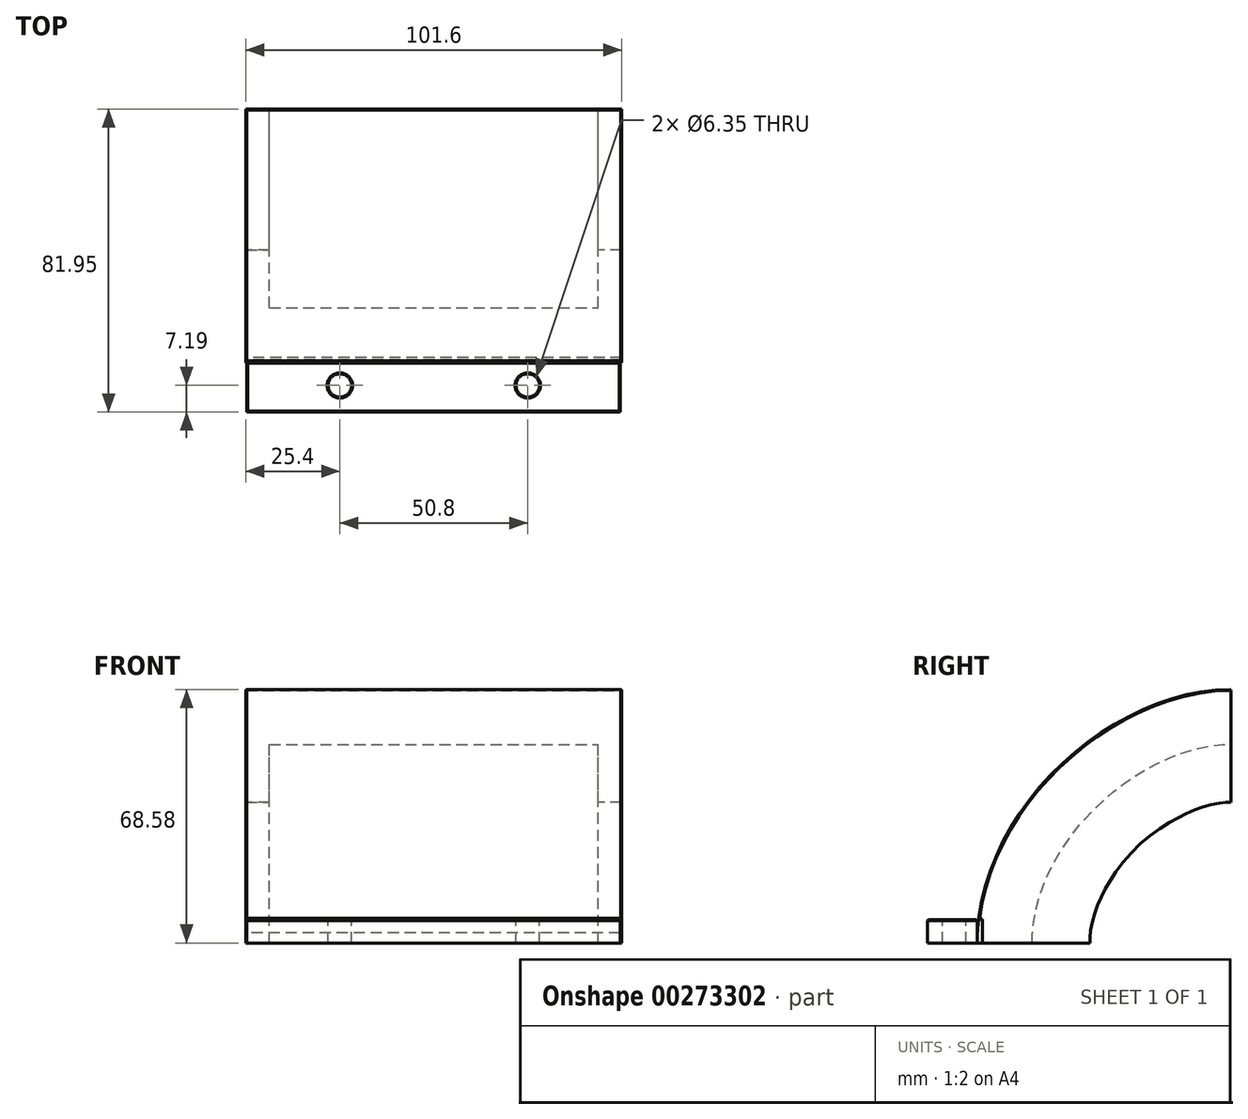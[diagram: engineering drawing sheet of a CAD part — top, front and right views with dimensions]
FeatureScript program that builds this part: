
annotation { "Feature Type Name" : "Feature", "Feature Type Description" : "" }
export const myFeature = defineFeature(function(context is Context, id is Id, definition is map)
    precondition{}
    {
        {
            var Q0;
            Q0=qCreatedBy(makeId("Right.planeOp"),FACE);
            var sketch = newSketch(context, id + "F0", { "sketchPlane" : qUnion([Q0])});
            skLineSegment(sketch, "E0", {"start": v(-36.59, 0) * mm, "end": v(-6.1, 0) * mm});
            skFitSpline(sketch, "E1", {"points": [v(-36.59, 0) * mm, v(32, 68.58) * mm], "startDerivative": vector(0.81, 109.5) * mm, "endDerivative": vector(95.98, 0.55) * mm});
            skLineSegment(sketch, "E2.bottom", {"start": v(-59.36, 6.45) * mm, "end": v(-35.21, 6.45) * mm});
            skLineSegment(sketch, "E2.top", {"start": v(-59.36, 0) * mm, "end": v(-35.21, 0) * mm});
            skLineSegment(sketch, "E2.left", {"start": v(-59.36, 6.45) * mm, "end": v(-59.36, 0) * mm});
            skLineSegment(sketch, "E2.right", {"start": v(-35.21, 6.45) * mm, "end": v(-35.21, 0) * mm});
            skFitSpline(sketch, "E3.0", {"points": [v(-6.1, -0.23) * mm, v(-6.1, 0.8) * mm, v(-5.96, 2.87) * mm, v(-5.36, 6.07) * mm, v(-4.35, 9.39) * mm, v(-2.9, 12.78) * mm, v(-1.04, 16.2) * mm, v(2, 20.7) * mm, v(6.72, 26.07) * mm, v(12.3, 30.58) * mm, v(16.95, 33.47) * mm, v(20.42, 35.23) * mm, v(23.8, 36.57) * mm, v(26.95, 37.49) * mm, v(29.8, 38) * mm, v(31.43, 38.1) * mm, v(32.17, 38.1) * mm]});
            skLineSegment(sketch, "E4", {"start": v(32, 38.1) * mm, "end": v(32, 68.58) * mm});
            skFitSpline(sketch, "E5.0", {"points": [v(-21.74, -0.11) * mm, v(-21.73, 0.72) * mm, v(-21.67, 2.4) * mm, v(-21.42, 4.89) * mm, v(-21.02, 7.37) * mm, v(-20.3, 10.68) * mm, v(-19.04, 14.78) * mm, v(-16.98, 19.63) * mm, v(-14.83, 23.56) * mm, v(-12.87, 26.62) * mm, v(-11.28, 28.87) * mm, v(-9.59, 31.06) * mm, v(-7.8, 33.18) * mm, v(-5.91, 35.22) * mm, v(-3.93, 37.2) * mm, v(-1.88, 39.09) * mm, v(0.24, 40.88) * mm, v(2.42, 42.57) * mm, v(4.66, 44.17) * mm, v(6.95, 45.66) * mm, v(9.26, 47.03) * mm, v(11.6, 48.28) * mm, v(14.74, 49.8) * mm, v(18.67, 51.36) * mm, v(22.54, 52.49) * mm, v(25.57, 53.12) * mm, v(27.8, 53.46) * mm, v(29.98, 53.67) * mm, v(31.38, 53.72) * mm, v(32.08, 53.73) * mm]});
            skSolve(sketch);
        }
        {
            var Q0;
            {var subQ0=sQuery(id+"F0.wireOp",EDGE,"E2.right");Q0=makeQuery(id+"F0.imprint","IMPRINT",FACE,{"disambiguationData":[TD([[makeQuery(id+"F0.imprint","IMPRINT",EDGE,{"derivedFrom":subQ0}),1.0]])]});}
            var Q1;
            {var subQ0=sQuery(id+"F0.wireOp",EDGE,"E3.0");var subQ1=sQuery(id+"F0.wireOp",EDGE,"E0");var subQ2=makeQuery(id+"F0.imprint","INTERSECT",VERTEX,{"derivedFrom":[subQ1,subQ0]});Q1=makeQuery(id+"F0.imprint","IMPRINT",FACE,{"disambiguationData":[TD([[makeQuery(id+"F0.imprint","IMPRINT",EDGE,{"disambiguationData":[TD([[subQ2,1.0]])],"derivedFrom":subQ1}),1.0]])]});}
            extrude(context, id + "F1", {"entities" : qUnion([Q0, Q1]), "endBound" : BoundingType.SYMMETRIC, "depth" : 101.6 * mm});
        }
        {
            var Q0;
            {var subQ5=sQuery(id+"F0.wireOp",EDGE,"E2.right");Q0=makeQuery(id+"F0.imprint","IMPRINT",FACE,{"disambiguationData":[TD([[makeQuery(id+"F0.imprint","IMPRINT",EDGE,{"derivedFrom":subQ5}),-1.0]])]});}
            extrude(context, id + "F2", {"entities" : qUnion([Q0]), "endBound" : BoundingType.SYMMETRIC, "depth" : 101.6 * mm});
        }
        {
            var Q0;
            {var subQ0=sQuery(id+"F0.wireOp",EDGE,"E3.0");var subQ1=sQuery(id+"F0.wireOp",EDGE,"E0");var subQ2=makeQuery(id+"F0.imprint","INTERSECT",VERTEX,{"derivedFrom":[subQ1,subQ0]});Q0=makeQuery(id+"F0.imprint","IMPRINT",FACE,{"disambiguationData":[TD([[makeQuery(id+"F0.imprint","IMPRINT",EDGE,{"disambiguationData":[TD([[subQ2,1.0]])],"derivedFrom":subQ1}),1.0]])]});}
            extrude(context, id + "F3", {"entities" : qUnion([Q0]), "operationType" : NewBodyOperationType.REMOVE, "endBound" : BoundingType.SYMMETRIC, "oppositeDirection" : true, "depth" : 88.9 * mm});
        }
        {
            var Q0;
            Q0=qCreatedBy(makeId("Top.planeOp"),FACE);
            var sketch = newSketch(context, id + "F4", { "sketchPlane" : qUnion([Q0])});
            skLineSegment(sketch, "E6.bottom", {"start": v(-50.53, -36.5) * mm, "end": v(50.35, -36.5) * mm});
            skLineSegment(sketch, "E6.top", {"start": v(-50.53, -49.96) * mm, "end": v(50.35, -49.96) * mm});
            skLineSegment(sketch, "E6.left", {"start": v(-50.53, -36.5) * mm, "end": v(-50.53, -49.96) * mm});
            skLineSegment(sketch, "E6.right", {"start": v(50.35, -36.5) * mm, "end": v(50.35, -49.96) * mm});
            skPoint(sketch, "E7", {"position": v(-28.94, -43.32) * mm});
            skPoint(sketch, "E8", {"position": v(28.76, -43.32) * mm});
            skSolve(sketch);
        }
        {
            var Q0;
            Q0 = qSketchRegion(id + "F4", true);
            extrude(context, id + "F5", {"entities" : qUnion([Q0]), "operationType" : NewBodyOperationType.ADD, "depth" : 6.35 * mm});
        }
        {
            var Q0;
            Q0=makeQuery(id+"F5.opExtrude","CAP_FACE",FACE,{"disambiguationData":[OSD([sQuery(id+"F4.wireOp",EDGE,"E6.bottom"),sQuery(id+"F4.wireOp",EDGE,"E6.top"),sQuery(id+"F4.wireOp",EDGE,"E6.left"),sQuery(id+"F4.wireOp",EDGE,"E6.right")])],"isStart":false});
            var sketch = newSketch(context, id + "F6", { "sketchPlane" : qUnion([Q0])});
            skPoint(sketch, "E9", {"position": v(-25.4, -42.77) * mm});
            skLineSegment(sketch, "E10.0.0", {"start": v(-50.53, -36.5) * mm, "end": v(-50.53, -49.96) * mm});
            skLineSegment(sketch, "E10.0.1", {"start": v(-50.53, -49.96) * mm, "end": v(50.35, -49.96) * mm});
            skLineSegment(sketch, "E10.0.2", {"start": v(50.35, -49.96) * mm, "end": v(50.35, -36.5) * mm});
            skLineSegment(sketch, "E10.0.3", {"start": v(50.35, -36.5) * mm, "end": v(-50.53, -36.5) * mm});
            skPoint(sketch, "E11", {"position": v(25.4, -42.77) * mm});
            skSolve(sketch);
        }
        {
            var Q0;
            Q0=sQuery(id+"F6.wireOp",VERTEX,"E9");
            var Q1;
            Q1=sQuery(id+"F6.wireOp",VERTEX,"E11");
            var Q2;
            Q2=makeQuery(id+"F2.opExtrude","SWEPT_BODY",BODY,{"disambiguationData":[OSD([sQuery(id+"F0.wireOp",EDGE,"E1"),sQuery(id+"F0.wireOp",EDGE,"E2.bottom"),sQuery(id+"F0.wireOp",EDGE,"E2.top"),sQuery(id+"F0.wireOp",EDGE,"E2.right")])]});
            hole(context, id + "F7", {"style" : HoleStyle.SIMPLE, "endStyle" : HoleEndStyle.THROUGH, "holeDiameter" : 6.35 * mm, "tappedDepth" : 12.7 * mm, "tapClearance" : 3, "startFromSketch" : true, "locations" : qUnion([Q0, Q1]), "scope" : qUnion([Q2])});
        }
        {
            var Q0;
            Q0=makeQuery(id+"F7.hole-0.boolean.opBoolean","COPY",EDGE,{"derivedFrom":makeQuery(id+"F7.hole-0.opRevolve","SWEPT_EDGE",EDGE,{"disambiguationData":[OSD([sQuery(id+"F7.hole-0.sketch.wireOp",EDGE,"core_line_2"),sQuery(id+"F7.hole-0.sketch.wireOp",EDGE,"core_line_3")])]})});
            var Q1;
            Q1=makeQuery(id+"F5.opExtrude","CAP_FACE",FACE,{"disambiguationData":[OSD([sQuery(id+"F4.wireOp",EDGE,"E6.bottom"),sQuery(id+"F4.wireOp",EDGE,"E6.top"),sQuery(id+"F4.wireOp",EDGE,"E6.left"),sQuery(id+"F4.wireOp",EDGE,"E6.right")])],"isStart":false});
            var Q2;
            Q2=makeQuery(id+"F1.opExtrude","SWEPT_FACE",FACE,{"disambiguationData":[OSD([sQuery(id+"F0.wireOp",EDGE,"E1")])]});
            chamfer(context, id + "F8", {"entities" : qUnion([Q0, Q1, Q2]), "width" : 0.25 * mm, "tangentPropagation" : true});
        }
    });
